# Revit family: Voila 4 Cuboid Surface
name_source: partatom
category: Lighting Fixtures
revit_build: Autodesk Revit Architecture 2015 (Build: 20140606_1530(x64)
units: mm (PartAtom-declared; Revit-internal decimal feet)

## types (1)
- Voila 4 Cuboid Surface
    120 Volts = Yes
    277 Volts = No
    347 Volts = No
    Apparent Load = 0 VA
    Baffle Position = 1 "
    Color Filter = 16777215
    Color Temperature = 0 K
    Conduit Feed = Yes
    Default Elevation = 48 "
    Dimming Lamp Color Temperature Shift = <None>
    Finish = Lumenwerx Standard White
    Fixture Height = 9 "
    Fixture Width = 4 "
    Lamp = LED
    Link to Product Page = http://lumenwerx.com
    Luminaire ID = VO4CS
    Manufacturer = Lumenwerx
    Model = Voila 4 Cuboid Surface
    Mounting Height = 1.5 "
    Optics = Lumenwerx CS Lens
    Photometric Web File = Generic
    Tilt Angle = -90.00°
    UNV 120 Volts-277 Volts = No
    URL = http://www.lumenwerx.com
    Voltage = 120 V

## geometry (parser evidence)
native form markers: Sweep x8
no freeform markers — native parametric forms only
